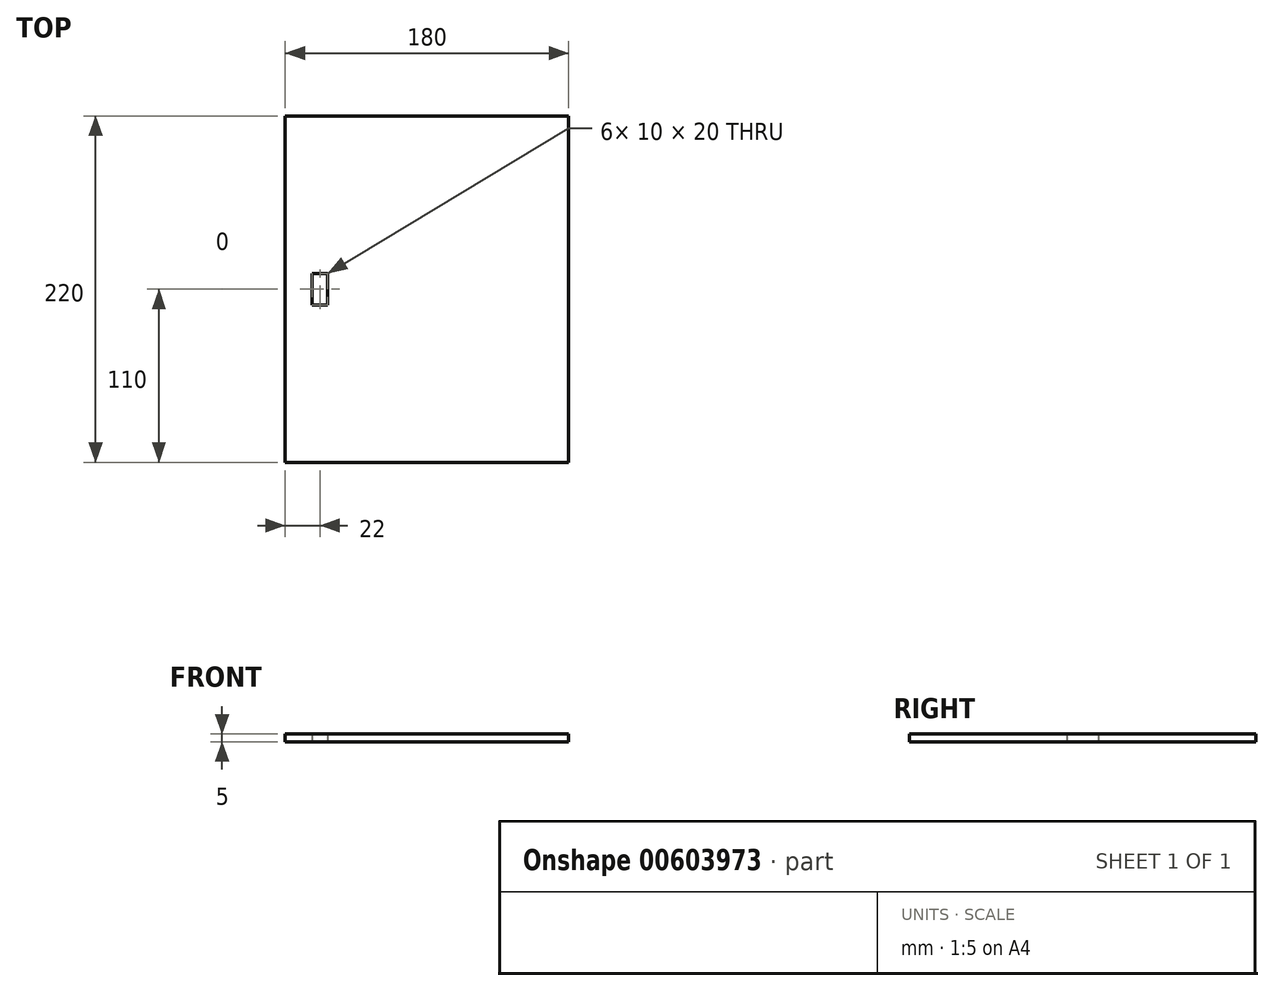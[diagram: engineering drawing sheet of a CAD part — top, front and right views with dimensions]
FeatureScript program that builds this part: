
annotation { "Feature Type Name" : "Feature", "Feature Type Description" : "" }
export const myFeature = defineFeature(function(context is Context, id is Id, definition is map)
    precondition{}
    {
        {
            var Q0;
            Q0=qCreatedBy(makeId("Top.planeOp"),FACE);
            var sketch = newSketch(context, id + "F0", { "sketchPlane" : qUnion([Q0])});
            skLineSegment(sketch, "E0.bottom", {"start": v(-90, 110) * mm, "end": v(90, 110) * mm});
            skLineSegment(sketch, "E0.top", {"start": v(-90, -110) * mm, "end": v(90, -110) * mm});
            skLineSegment(sketch, "E0.left", {"start": v(-90, 110) * mm, "end": v(-90, -110) * mm});
            skLineSegment(sketch, "E0.right", {"start": v(90, 110) * mm, "end": v(90, -110) * mm});
            skPoint(sketch, "E0.middle", {"position": v(0, 0) * mm});
            skLineSegment(sketch, "E1.bottom", {"start": v(-73, 10) * mm, "end": v(-63, 10) * mm});
            skLineSegment(sketch, "E1.top", {"start": v(-73, -10) * mm, "end": v(-63, -10) * mm});
            skLineSegment(sketch, "E1.left", {"start": v(-73, 10) * mm, "end": v(-73, -10) * mm});
            skLineSegment(sketch, "E1.right", {"start": v(-63, 10) * mm, "end": v(-63, -10) * mm});
            skPoint(sketch, "E1.middle", {"position": v(-68, 0) * mm});
            skSolve(sketch);
        }
        {
            var Q0;
            Q0=makeQuery(id+"F0.imprint","IMPRINT",FACE,{"disambiguationData":[TD([[makeQuery(id+"F0.imprint","IMPRINT",EDGE,{"derivedFrom":sQuery(id+"F0.wireOp",EDGE,"E0.bottom")}),-1.0]])]});
            extrude(context, id + "F1", {"entities" : qUnion([Q0]), "depth" : 5 * mm, "offsetDistance" : 25 * mm});
        }
    });
